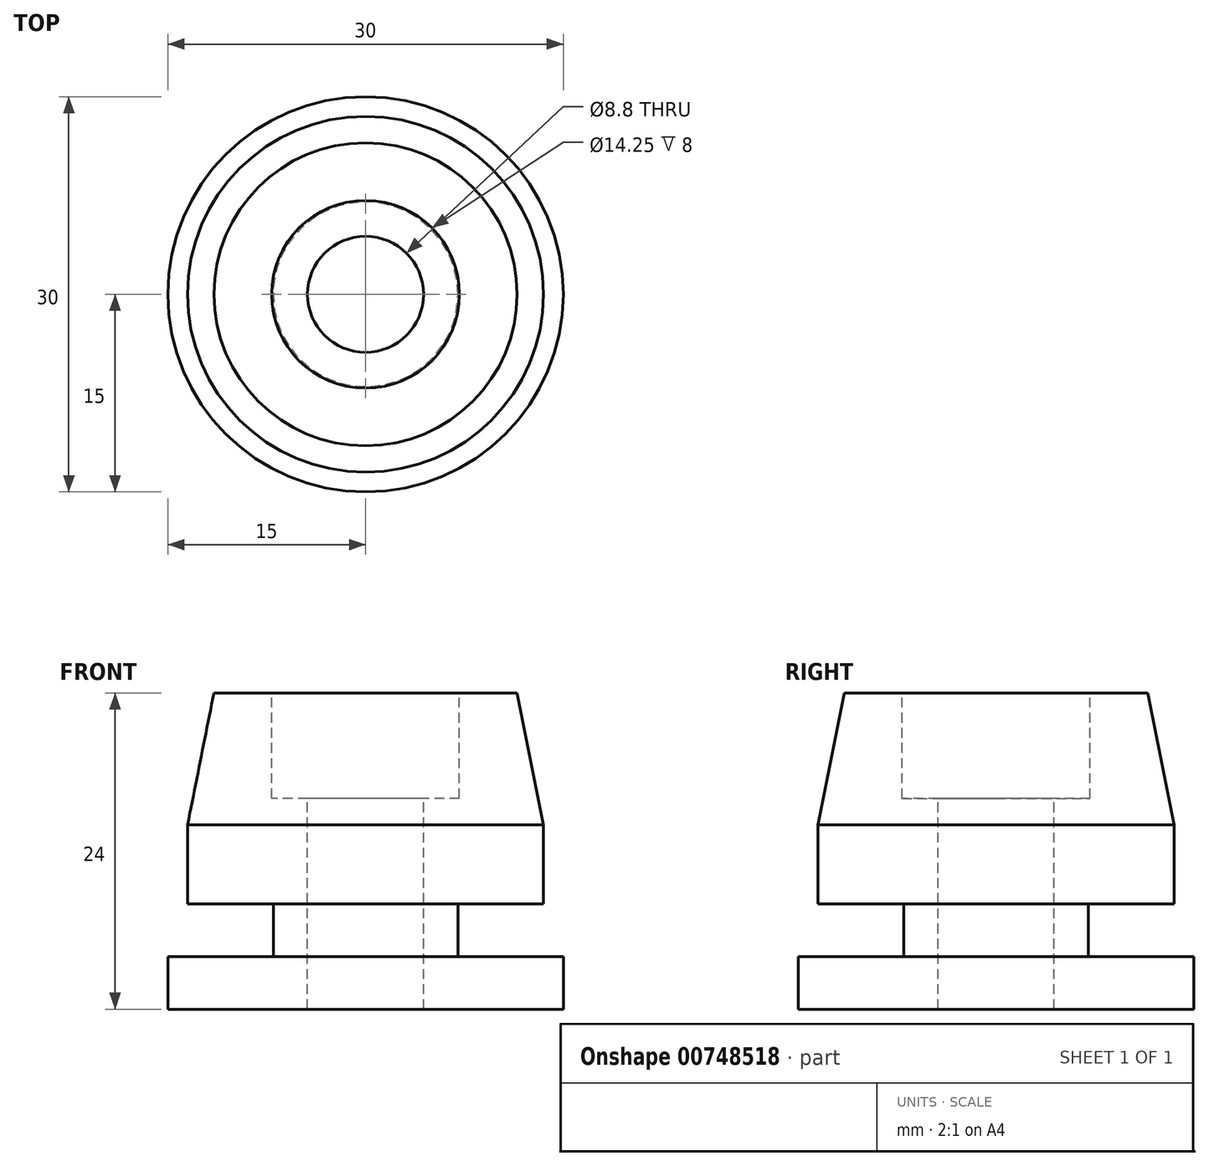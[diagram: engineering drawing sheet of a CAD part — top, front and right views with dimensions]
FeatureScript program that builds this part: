
annotation { "Feature Type Name" : "Feature", "Feature Type Description" : "" }
export const myFeature = defineFeature(function(context is Context, id is Id, definition is map)
    precondition{}
    {
        {
            var Q0;
            Q0=qCreatedBy(makeId("Front.planeOp"),FACE);
            var sketch = newSketch(context, id + "F0", { "sketchPlane" : qUnion([Q0])});
            skLineSegment(sketch, "E0", {"start": v(0, 0) * mm, "end": v(-15, 0) * mm});
            skLineSegment(sketch, "E1", {"start": v(-15, 0) * mm, "end": v(-15, 4) * mm});
            skLineSegment(sketch, "E2", {"start": v(-15, 4) * mm, "end": v(-7, 4) * mm});
            skLineSegment(sketch, "E3", {"start": v(-7, 4) * mm, "end": v(-7, 8) * mm});
            skLineSegment(sketch, "E4", {"start": v(-7, 8) * mm, "end": v(-13.5, 8) * mm});
            skLineSegment(sketch, "E5", {"start": v(-13.5, 8) * mm, "end": v(-13.5, 24) * mm});
            skLineSegment(sketch, "E6", {"start": v(-13.5, 24) * mm, "end": v(0, 24) * mm});
            skLineSegment(sketch, "E7", {"start": v(0, 24) * mm, "end": v(0, 0) * mm});
            skSolve(sketch);
        }
        {
            var Q0;
            Q0=makeQuery(id+"F0.imprint","IMPRINT",FACE,{"disambiguationData":[TD([[makeQuery(id+"F0.imprint","IMPRINT",EDGE,{"derivedFrom":sQuery(id+"F0.wireOp",EDGE,"E0")}),-1.0]])]});
            var Q1;
            Q1=sQuery(id+"F0.wireOp",EDGE,"E7");
            revolve(context, id + "F1", {"surfaceOperationType" : NewSurfaceOperationType.NEW, "entities" : qUnion([Q0]), "axis" : qUnion([Q1]), "revolveType" : RevolveType.FULL});
        }
        {
            var Q0;
            Q0=makeQuery(id+"F1.opRevolve","SWEPT_EDGE",EDGE,{"disambiguationData":[OSD([sQuery(id+"F0.wireOp",EDGE,"E5"),sQuery(id+"F0.wireOp",EDGE,"E6")])]});
            chamfer(context, id + "F2", {"entities" : qUnion([Q0]), "chamferType" : ChamferType.TWO_OFFSETS, "width1" : 2 * mm, "oppositeDirection" : false, "width2" : 10 * mm, "tangentPropagation" : true});
        }
        {
            var Q0;
            Q0=makeQuery(id+"F1.opRevolve","SWEPT_FACE",FACE,{"disambiguationData":[OSD([sQuery(id+"F0.wireOp",EDGE,"E6")])]});
            var sketch = newSketch(context, id + "F3", { "sketchPlane" : qUnion([Q0])});
            skPoint(sketch, "E8", {"position": v(0, 0) * mm});
            skSolve(sketch);
        }
        {
            var Q0;
            Q0=sQuery(id+"F3.wireOp",VERTEX,"E8");
            var Q1;
            Q1=makeQuery(id+"F1.opRevolve","SWEPT_BODY",BODY,{"disambiguationData":[OSD([sQuery(id+"F0.wireOp",EDGE,"E0"),sQuery(id+"F0.wireOp",EDGE,"E1"),sQuery(id+"F0.wireOp",EDGE,"E2"),sQuery(id+"F0.wireOp",EDGE,"E3"),sQuery(id+"F0.wireOp",EDGE,"E4"),sQuery(id+"F0.wireOp",EDGE,"E5"),sQuery(id+"F0.wireOp",EDGE,"E6"),sQuery(id+"F0.wireOp",EDGE,"E7")])]});
            hole(context, id + "F4", {"style" : HoleStyle.C_BORE, "endStyle" : HoleEndStyle.THROUGH, "standardTappedOrClearance" : lookupTablePath({ "standard" : "ISO", "fit" : "Normal", "size" : "M8", "type" : "Clearance" }), "standardBlindInLast" : lookupTablePath({ "fit" : "Standard", "standard" : "ISO", "size" : "M8", "type" : "Clearance" }), "holeDiameter" : 8.8 * mm, "cBoreDiameter" : 14.25 * mm, "cBoreDepth" : 8 * mm, "majorDiameter" : 5 * mm, "isTappedThrough" : true, "tappedDepth" : 12 * mm, "tapClearance" : 3, "locations" : qUnion([Q0]), "scope" : qUnion([Q1])});
        }
    });
